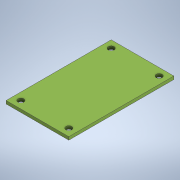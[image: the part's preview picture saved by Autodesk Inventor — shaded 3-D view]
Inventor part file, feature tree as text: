
AUTODESK INVENTOR PART (.ipt)
format: ipt  version: 2021 (Build 250183000, 183)  size: 108,544 bytes
history: native  units: mm
features: extrude x1, sketch x1
ambient origin geometry x8: Origin, YZ Plane, XZ Plane, XY Plane, X Axis, Y Axis, Z Axis, Center Point
bodies: Solid1 (feature_tree)
feature tree (2):
  extrude  "Extrusion1"  Depth=57.0mm
  sketch  "Sketch1"  dims[d0=34.0mm d1=57.0mm d2=26.0mm d3=49.0mm d4=3.2mm d5=3.2mm d6=3.2mm d7=3.2mm d8=1.65mm d9=0.0mm]
